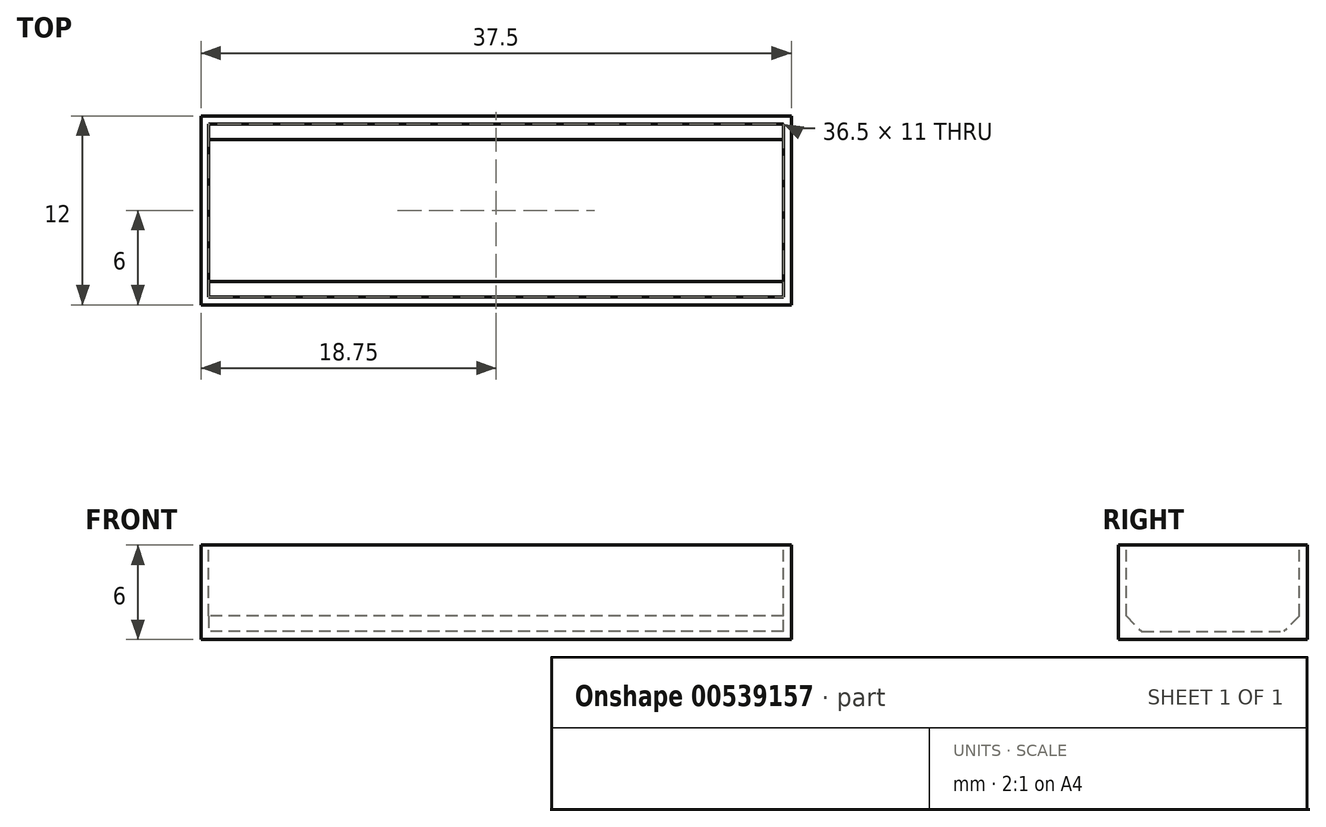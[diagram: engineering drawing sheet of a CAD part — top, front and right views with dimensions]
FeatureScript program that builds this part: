
annotation { "Feature Type Name" : "Feature", "Feature Type Description" : "" }
export const myFeature = defineFeature(function(context is Context, id is Id, definition is map)
    precondition{}
    {
        {
            var Q0;
            Q0=qCreatedBy(makeId("Top.planeOp"),FACE);
            var sketch = newSketch(context, id + "F0", { "sketchPlane" : qUnion([Q0])});
            skLineSegment(sketch, "E0.bottom", {"start": v(0, 0) * mm, "end": v(37.5, 0) * mm});
            skLineSegment(sketch, "E0.top", {"start": v(0, 12) * mm, "end": v(37.5, 12) * mm});
            skLineSegment(sketch, "E0.left", {"start": v(0, 0) * mm, "end": v(0, 12) * mm});
            skLineSegment(sketch, "E0.right", {"start": v(37.5, 0) * mm, "end": v(37.5, 12) * mm});
            skSolve(sketch);
        }
        {
            var Q0;
            Q0=qSketchRegion(id+"F0",true);
            extrude(context, id + "F1", {"entities" : qUnion([Q0]), "depth" : 6 * mm, "offsetDistance" : 25 * mm});
        }
        {
            var Q0;
            Q0=makeQuery(id+"F1.opExtrude","CAP_FACE",FACE,{"disambiguationData":[OSD([sQuery(id+"F0.wireOp",EDGE,"E0.bottom"),sQuery(id+"F0.wireOp",EDGE,"E0.top"),sQuery(id+"F0.wireOp",EDGE,"E0.left"),sQuery(id+"F0.wireOp",EDGE,"E0.right")])],"isStart":false});
            var sketch = newSketch(context, id + "F2", { "sketchPlane" : qUnion([Q0])});
            skLineSegment(sketch, "E1.bottom", {"start": v(0.5, 0.5) * mm, "end": v(37, 0.5) * mm});
            skLineSegment(sketch, "E1.top", {"start": v(0.5, 11.5) * mm, "end": v(37, 11.5) * mm});
            skLineSegment(sketch, "E1.left", {"start": v(0.5, 0.5) * mm, "end": v(0.5, 11.5) * mm});
            skLineSegment(sketch, "E1.right", {"start": v(37, 0.5) * mm, "end": v(37, 11.5) * mm});
            skSolve(sketch);
        }
        {
            var Q0;
            Q0=qSketchRegion(id+"F2",true);
            extrude(context, id + "F3", {"entities" : qUnion([Q0]), "operationType" : NewBodyOperationType.REMOVE, "oppositeDirection" : true, "depth" : 5.5 * mm, "offsetDistance" : 25 * mm});
        }
        {
            var Q0;
            Q0=makeQuery(id+"F3.boolean.opBoolean","COPY",EDGE,{"derivedFrom":makeQuery(id+"F3.opExtrude","CAP_EDGE",EDGE,{"disambiguationData":[OSD([sQuery(id+"F2.wireOp",EDGE,"E1.top")])],"isStart":false})});
            var Q1;
            Q1=makeQuery(id+"F3.boolean.opBoolean","COPY",EDGE,{"derivedFrom":makeQuery(id+"F3.opExtrude","CAP_EDGE",EDGE,{"disambiguationData":[OSD([sQuery(id+"F2.wireOp",EDGE,"E1.bottom")])],"isStart":false})});
            chamfer(context, id + "F4", {"entities" : qUnion([Q0, Q1]), "width" : 1 * mm, "tangentPropagation" : true});
        }
    });
